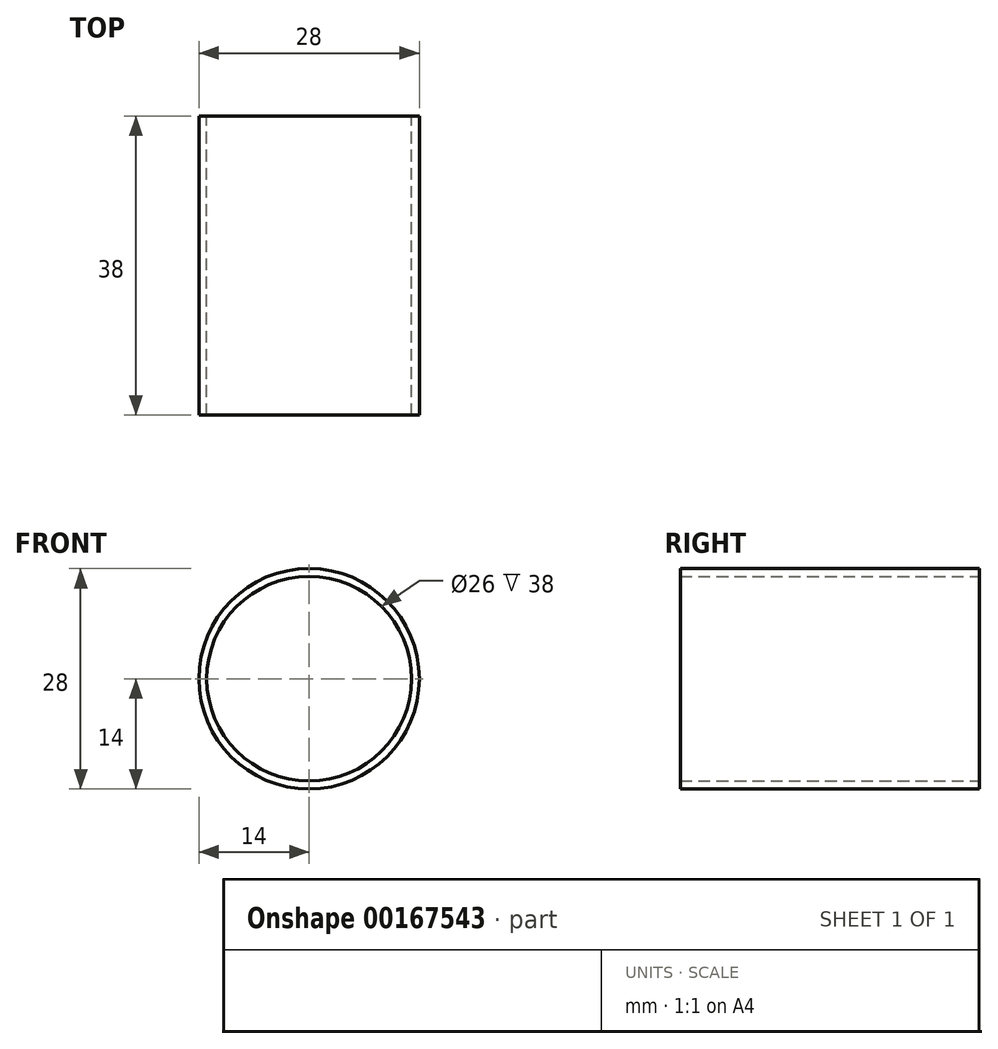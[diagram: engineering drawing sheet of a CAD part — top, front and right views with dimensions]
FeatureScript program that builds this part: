
annotation { "Feature Type Name" : "Feature", "Feature Type Description" : "" }
export const myFeature = defineFeature(function(context is Context, id is Id, definition is map)
    precondition{}
    {
        {
            var Q0;
            Q0=qCreatedBy(makeId("Front.planeOp"),FACE);
            var sketch = newSketch(context, id + "F0", { "sketchPlane" : qUnion([Q0])});
            skCircle(sketch, "E0", {"center": v(0, 0) * mm, "radius": 14 * mm});
            skCircle(sketch, "E1", {"center": v(0, 0) * mm, "radius": 13 * mm});
            skSolve(sketch);
        }
        {
            var Q0;
            Q0=qSketchRegion(id+"F0",true);
            extrude(context, id + "F1", {"entities" : qUnion([Q0]), "depth" : 38 * mm, "symmetric" : true});
        }
    });
